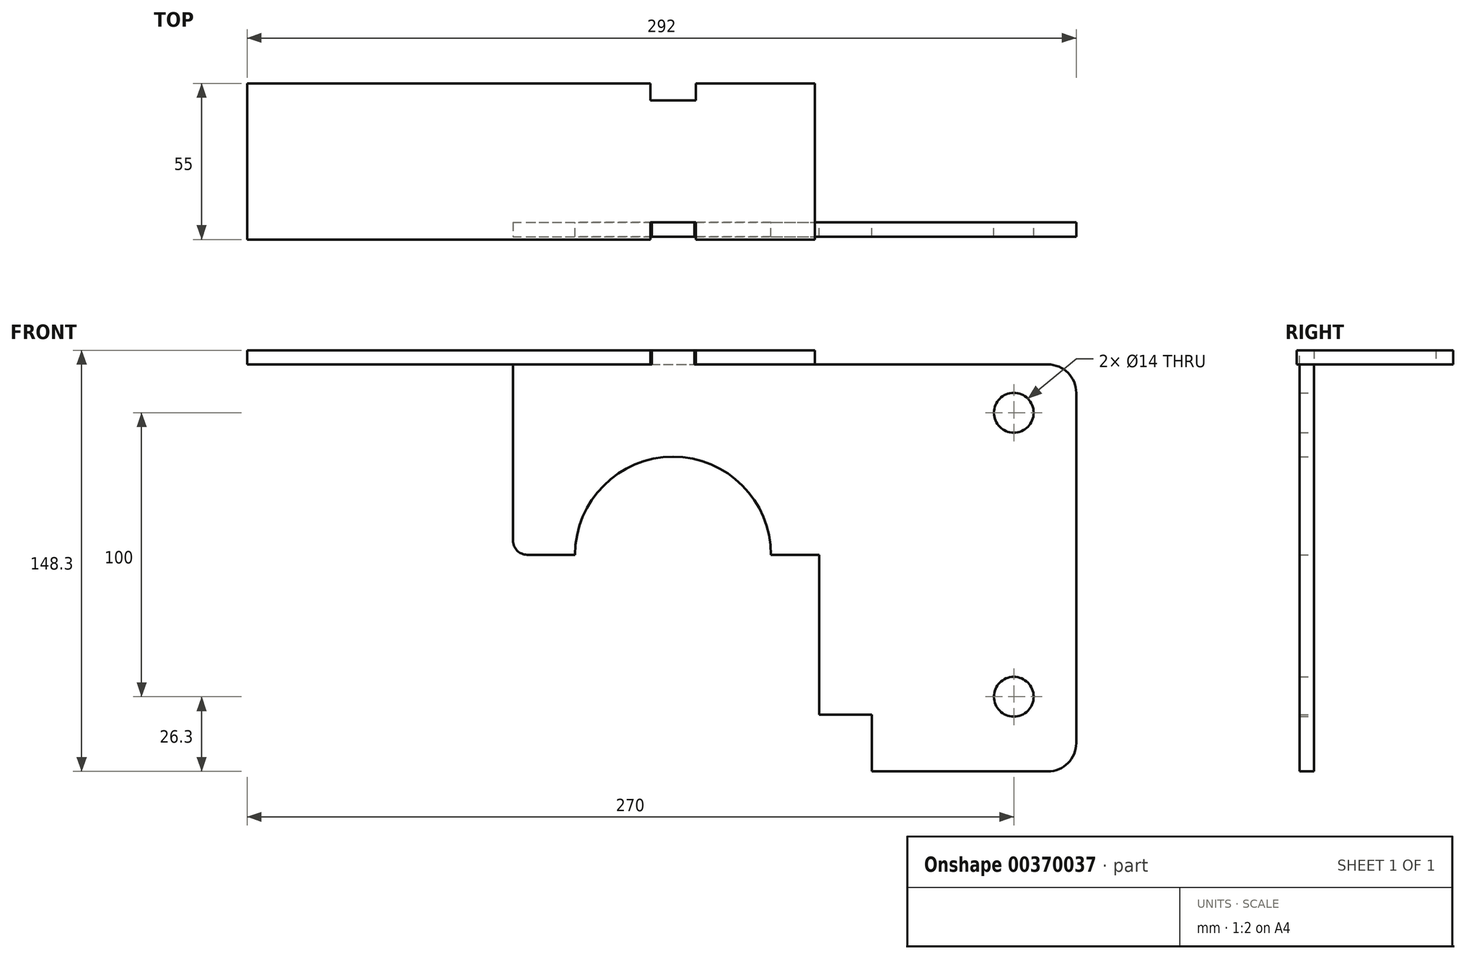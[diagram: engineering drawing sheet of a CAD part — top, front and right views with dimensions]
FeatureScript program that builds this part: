
annotation { "Feature Type Name" : "Feature", "Feature Type Description" : "" }
export const myFeature = defineFeature(function(context is Context, id is Id, definition is map)
    precondition{}
    {
        {
            var Q0;
            Q0=qCreatedBy(makeId("Front.planeOp"),FACE);
            var sketch = newSketch(context, id + "F0", { "sketchPlane" : qUnion([Q0])});
            skCircle(sketch, "E0", {"center": v(0, 0) * mm, "radius": 34.5 * mm, "construction": true});
            skLineSegment(sketch, "E1", {"start": v(-112.49, 67) * mm, "end": v(132, 67) * mm});
            skLineSegment(sketch, "E2", {"start": v(142, 57) * mm, "end": v(142, -66.3) * mm});
            skLineSegment(sketch, "E3", {"start": v(132, -76.3) * mm, "end": v(70, -76.3) * mm});
            skLineSegment(sketch, "E4", {"start": v(34.5, 0) * mm, "end": v(34.5, 0) * mm});
            skLineSegment(sketch, "E5", {"start": v(-56.37, 0) * mm, "end": v(-34.5, 0) * mm});
            skCircle(sketch, "E6", {"center": v(120, 50) * mm, "radius": 7 * mm});
            skCircle(sketch, "E7", {"center": v(120, -50) * mm, "radius": 7 * mm});
            skArc(sketch, "E8", {"start": v(34.5, 0) * mm, "mid": v(0, 34.5) * mm, "end": v(-34.5, 0) * mm});
            skLineSegment(sketch, "E9", {"start": v(34.5, 0) * mm, "end": v(51.5, 0) * mm});
            skPoint(sketch, "E10", {"position": v(51.5, 0) * mm});
            skLineSegment(sketch, "E11", {"start": v(51.5, 0) * mm, "end": v(51.5, -56.3) * mm});
            skLineSegment(sketch, "E12", {"start": v(51.5, -56.3) * mm, "end": v(70, -56.3) * mm});
            skLineSegment(sketch, "E13", {"start": v(70, -56.3) * mm, "end": v(70, -76.3) * mm});
            skLineSegment(sketch, "E14.bottom", {"start": v(-7.5, 67) * mm, "end": v(7.5, 67) * mm});
            skLineSegment(sketch, "E14.top", {"start": v(-7.5, 72) * mm, "end": v(7.5, 72) * mm});
            skLineSegment(sketch, "E14.left", {"start": v(-7.5, 67) * mm, "end": v(-7.5, 72) * mm});
            skLineSegment(sketch, "E14.right", {"start": v(7.5, 67) * mm, "end": v(7.5, 72) * mm});
            skPoint(sketch, "E15", {"position": v(0, 72) * mm});
            skPoint(sketch, "E16.visualSharp", {"position": v(142, 67) * mm});
            skArc(sketch, "E16.filletArc", {"start": v(142, 57) * mm, "mid": v(139.07, 64.07) * mm, "end": v(132, 67) * mm});
            skPoint(sketch, "E17.visualSharp", {"position": v(142, -76.3) * mm});
            skArc(sketch, "E17.filletArc", {"start": v(132, -76.3) * mm, "mid": v(139.07, -73.37) * mm, "end": v(142, -66.3) * mm});
            skLineSegment(sketch, "E18", {"start": v(-118.9, 49.33) * mm, "end": v(-62.79, 2.33) * mm});
            skPoint(sketch, "E19.visualSharp", {"position": v(-140, 67) * mm});
            skArc(sketch, "E19.filletArc", {"start": v(-112.49, 67) * mm, "mid": v(-121.88, 60.42) * mm, "end": v(-118.9, 49.33) * mm});
            skPoint(sketch, "E20.visualSharp", {"position": v(-60, 0) * mm});
            skArc(sketch, "E20.filletArc", {"start": v(-62.79, 2.33) * mm, "mid": v(-59.78, 0.6) * mm, "end": v(-56.37, 0) * mm});
            skSolve(sketch);
        }
        {
            var Q0;
            Q0=qSketchRegion(id+"F0",true);
            extrude(context, id + "F1", {"entities" : qUnion([Q0]), "depth" : 5 * mm});
        }
        {
            var Q0;
            {var subQ0=sQuery(id+"F0.wireOp",EDGE,"E1");Q0=makeQuery(id+"F1.opExtrude","SWEPT_FACE",FACE,{"disambiguationData":[OSD([subQ0]),TDD([makeQuery(id+"F0.imprint","IMPRINT",EDGE,{"disambiguationData":[TD([[makeQuery(id+"F0.imprint","INTERSECT",VERTEX,{"derivedFrom":[sQuery(id+"F0.wireOp",EDGE,"Qq6vzx61-vcA7-Or1N-aunF-YzaSUn9qJwvq"),subQ0]}),-1.0]])],"derivedFrom":subQ0})])]});}
            var sketch = newSketch(context, id + "F2", { "sketchPlane" : qUnion([Q0])});
            skLineSegment(sketch, "E21.bottom", {"start": v(50, -6) * mm, "end": v(8, -6) * mm});
            skLineSegment(sketch, "E21.top", {"start": v(50, 49) * mm, "end": v(8, 49) * mm});
            skLineSegment(sketch, "E21.left", {"start": v(50, -6) * mm, "end": v(50, 49) * mm});
            skLineSegment(sketch, "E21.right", {"start": v(-150, -6) * mm, "end": v(-150, 49) * mm});
            skLineSegment(sketch, "E22.top", {"start": v(-8, 0) * mm, "end": v(8, 0) * mm});
            skLineSegment(sketch, "E22.left", {"start": v(-8, -6) * mm, "end": v(-8, 0) * mm});
            skLineSegment(sketch, "E22.right", {"start": v(8, -6) * mm, "end": v(8, 0) * mm});
            skLineSegment(sketch, "E23.trimOffspring", {"start": v(-8, -6) * mm, "end": v(-150, -6) * mm});
            skLineSegment(sketch, "E24.top", {"start": v(-8, 43) * mm, "end": v(8, 43) * mm});
            skLineSegment(sketch, "E24.left", {"start": v(-8, 49) * mm, "end": v(-8, 43) * mm});
            skLineSegment(sketch, "E24.right", {"start": v(8, 49) * mm, "end": v(8, 43) * mm});
            skLineSegment(sketch, "E25.trimOffspring", {"start": v(-8, 49) * mm, "end": v(-150, 49) * mm});
            skSolve(sketch);
        }
        {
            var Q0;
            Q0=qSketchRegion(id+"F2",true);
            extrude(context, id + "F3", {"entities" : qUnion([Q0]), "depth" : 5 * mm});
        }
        {
            var Q0;
            Q0=makeQuery(id+"F1.opExtrude","CAP_FACE",FACE,{"disambiguationData":[OSD([sQuery(id+"F0.wireOp",EDGE,"Qq6vzx61-vcA7-Or1N-aunF-YzaSUn9qJwvq"),sQuery(id+"F0.wireOp",EDGE,"E1"),sQuery(id+"F0.wireOp",EDGE,"E2"),sQuery(id+"F0.wireOp",EDGE,"E3"),sQuery(id+"F0.wireOp",EDGE,"E5"),sQuery(id+"F0.wireOp",EDGE,"E6"),sQuery(id+"F0.wireOp",EDGE,"E7"),sQuery(id+"F0.wireOp",EDGE,"E8"),sQuery(id+"F0.wireOp",EDGE,"E9"),sQuery(id+"F0.wireOp",EDGE,"E11"),sQuery(id+"F0.wireOp",EDGE,"E12"),sQuery(id+"F0.wireOp",EDGE,"E13"),sQuery(id+"F0.wireOp",EDGE,"E14.top"),sQuery(id+"F0.wireOp",EDGE,"E14.left"),sQuery(id+"F0.wireOp",EDGE,"E14.right"),sQuery(id+"F0.wireOp",EDGE,"E16.filletArc"),sQuery(id+"F0.wireOp",EDGE,"E17.filletArc")])],"isStart":false});
            var sketch = newSketch(context, id + "F4", { "sketchPlane" : qUnion([Q0])});
            skLineSegment(sketch, "E26", {"start": v(-56.37, 0) * mm, "end": v(-56.37, 67) * mm});
            skPoint(sketch, "E26.endSnap0", {"position": v(-60, 67) * mm});
            skLineSegment(sketch, "E27.0", {"start": v(-112.49, 67) * mm, "end": v(-7.5, 67) * mm});
            skArc(sketch, "E28.0", {"start": v(-112.49, 67) * mm, "mid": v(-121.88, 60.42) * mm, "end": v(-118.9, 49.33) * mm});
            skLineSegment(sketch, "E29.0", {"start": v(-118.9, 49.33) * mm, "end": v(-62.79, 2.33) * mm});
            skArc(sketch, "E30.0", {"start": v(-62.79, 2.33) * mm, "mid": v(-59.78, 0.6) * mm, "end": v(-56.37, 0) * mm});
            skSolve(sketch);
        }
        {
            var Q0;
            Q0 = qSketchRegion(id + "F4", true);
            extrude(context, id + "F5", {"entities" : qUnion([Q0]), "operationType" : NewBodyOperationType.REMOVE, "oppositeDirection" : true, "depth" : 25 * mm});
        }
        {
            var Q0;
            Q0=makeQuery(id+"F5.boolean.opBoolean","COPY",EDGE,{"derivedFrom":makeQuery(id+"F5.opExtrude","SWEPT_EDGE",EDGE,{"disambiguationData":[OSD([sQuery(id+"F4.wireOp",EDGE,"E26"),sQuery(id+"F4.wireOp",EDGE,"E27.0")])]})});
            var Q1;
            {var subQ0=sQuery(id+"F0.wireOp",EDGE,"E5");Q1=makeQuery(id+"F5.boolean.opBoolean","MERGE",EDGE,{"derivedFrom":[makeQuery(id+"F1.opExtrude","SWEPT_EDGE",EDGE,{"disambiguationData":[OSD([subQ0,sQuery(id+"F0.wireOp",EDGE,"E20.filletArc")])]}),makeQuery(id+"F5.opExtrude","SWEPT_EDGE",EDGE,{"disambiguationData":[OSD([subQ0,sQuery(id+"F4.wireOp",EDGE,"E26"),sQuery(id+"F4.wireOp",EDGE,"E30.0")])]})]});}
            fillet(context, id + "F6", {"entities" : qUnion([Q0, Q1]), "radius" : 5 * mm, "tangentPropagation" : true, "allowEdgeOverflow" : false});
        }
    });
